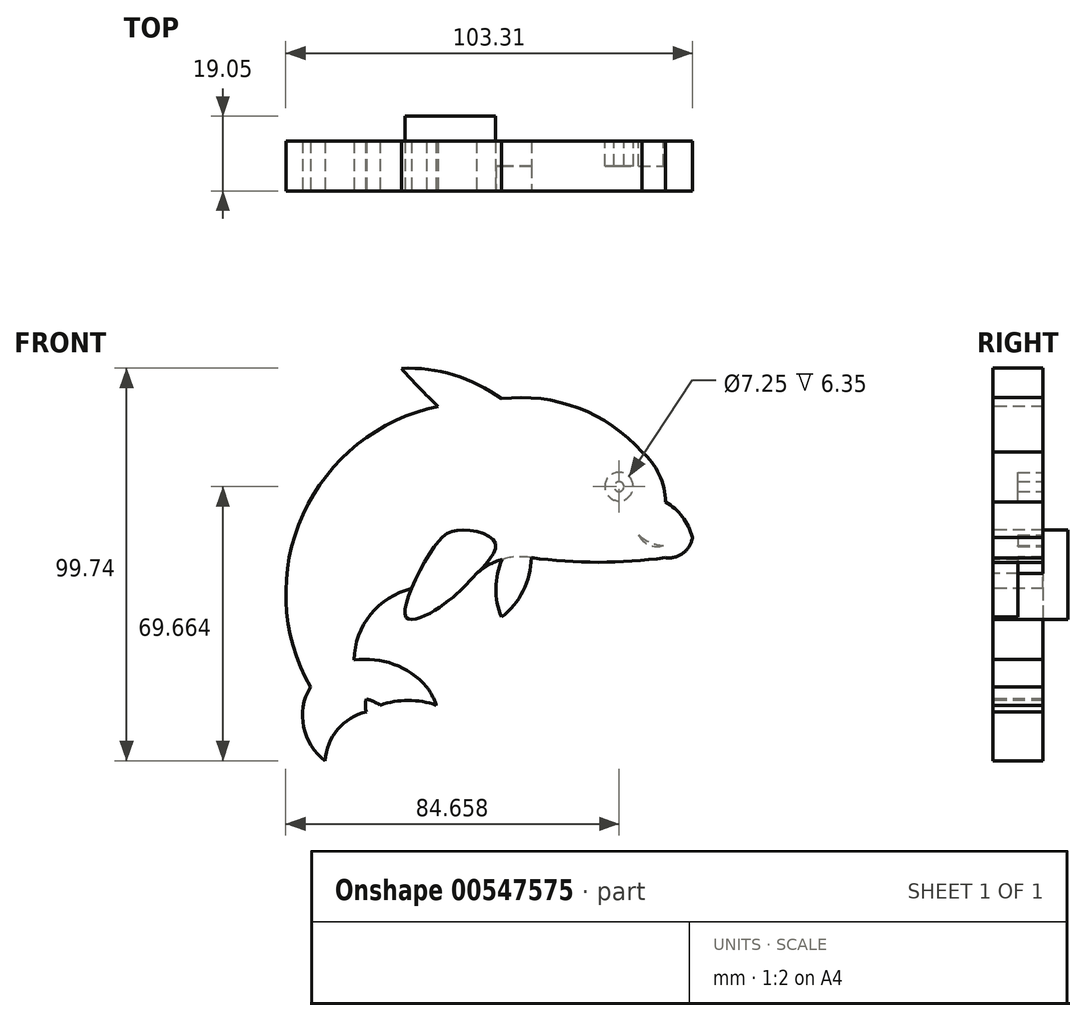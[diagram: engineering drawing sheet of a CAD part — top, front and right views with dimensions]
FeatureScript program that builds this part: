
annotation { "Feature Type Name" : "Feature", "Feature Type Description" : "" }
export const myFeature = defineFeature(function(context is Context, id is Id, definition is map)
    precondition{}
    {
        {
            var Q0;
            Q0=qCreatedBy(makeId("Front.planeOp"),FACE);
            var sketch = newSketch(context, id + "F0", { "sketchPlane" : qUnion([Q0])});
            skArc(sketch, "E0", {"start": v(-21.74, 57.63) * mm, "mid": v(-17.2, 52.68) * mm, "end": v(-12.41, 47.99) * mm});
            skArc(sketch, "E1", {"start": v(3.68, 49.92) * mm, "mid": v(-8.37, 55.95) * mm, "end": v(-21.74, 57.63) * mm});
            skArc(sketch, "E2", {"start": v(39.42, 36.38) * mm, "mid": v(23.22, 47.55) * mm, "end": v(3.68, 49.92) * mm});
            skArc(sketch, "E3", {"start": v(45.32, 23.7) * mm, "mid": v(43.74, 30.68) * mm, "end": v(39.42, 36.38) * mm});
            skArc(sketch, "E4", {"start": v(52.19, 14.71) * mm, "mid": v(49.66, 19.9) * mm, "end": v(45.32, 23.7) * mm});
            skArc(sketch, "E5", {"start": v(45.32, 9.53) * mm, "mid": v(49.83, 10.7) * mm, "end": v(52.19, 14.71) * mm});
            skArc(sketch, "E6", {"start": v(11.27, 9.53) * mm, "mid": v(28.3, 8.38) * mm, "end": v(45.32, 9.53) * mm});
            skArc(sketch, "E7", {"start": v(3.68, -5.58) * mm, "mid": v(9.2, 1.11) * mm, "end": v(11.27, 9.53) * mm});
            skArc(sketch, "E8", {"start": v(3.85, 9.11) * mm, "mid": v(2.26, 1.78) * mm, "end": v(3.68, -5.58) * mm});
            skArc(sketch, "E9", {"start": v(11.27, 9.53) * mm, "mid": v(3.85, 9.11) * mm, "end": v(-2.62, 5.46) * mm});
            skFitSpline(sketch, "E10", {"points": [v(-2.62, 5.46) * mm, v(-8.07, 0) * mm, v(-16.67, -5.6) * mm, v(-20.7, -5.31) * mm, v(-13.95, 11.58) * mm, v(-6.56, 16.6) * mm, v(2.08, 13.23) * mm, v(-2.62, 5.46) * mm]});
            skArc(sketch, "E11", {"start": v(-19.2, 1.68) * mm, "mid": v(-29.6, -4.9) * mm, "end": v(-33.76, -16.47) * mm});
            skArc(sketch, "E12", {"start": v(-15.33, -23.25) * mm, "mid": v(-23.7, -17.54) * mm, "end": v(-33.76, -16.47) * mm});
            skArc(sketch, "E13", {"start": v(-12.9, -27.95) * mm, "mid": v(-13.93, -25.5) * mm, "end": v(-15.33, -23.25) * mm});
            skArc(sketch, "E14", {"start": v(-12.9, -27.95) * mm, "mid": v(-20.03, -26.73) * mm, "end": v(-27.16, -27.95) * mm});
            skArc(sketch, "E15", {"start": v(-27.16, -27.95) * mm, "mid": v(-28.82, -27) * mm, "end": v(-30.64, -26.38) * mm});
            skArc(sketch, "E16", {"start": v(-30.64, -26.38) * mm, "mid": v(-30.9, -28) * mm, "end": v(-30.64, -29.62) * mm});
            skArc(sketch, "E17", {"start": v(-30.64, -29.62) * mm, "mid": v(-37.96, -34.09) * mm, "end": v(-41.1, -42.07) * mm});
            skArc(sketch, "E18", {"start": v(-44.9, -23.37) * mm, "mid": v(-46.6, -33.45) * mm, "end": v(-41.1, -42.07) * mm});
            skArc(sketch, "E19", {"start": v(-12.41, 47.99) * mm, "mid": v(-46.75, 20.55) * mm, "end": v(-44.9, -23.37) * mm});
            skSolve(sketch);
        }
        {
            var Q0;
            Q0=makeQuery(id+"F0.imprint","IMPRINT",FACE,{"disambiguationData":[TD([[makeQuery(id+"F0.imprint","IMPRINT",EDGE,{"derivedFrom":sQuery(id+"F0.wireOp",EDGE,"E0")}),1.0]])]});
            extrude(context, id + "F1", {"entities" : qUnion([Q0]), "oppositeDirection" : true, "depth" : 12.7 * mm, "offsetDistance" : 25.4 * mm});
        }
        {
            var Q0;
            {var subQ0=sQuery(id+"F0.wireOp",EDGE,"E10");var subQ1=makeQuery(id+"F0.imprint","INTERSECT",VERTEX,{"derivedFrom":[sQuery(id+"F0.wireOp",EDGE,"E9"),subQ0]});Q0=makeQuery(id+"F0.imprint","IMPRINT",FACE,{"disambiguationData":[TD([[makeQuery(id+"F0.imprint","IMPRINT",EDGE,{"disambiguationData":[TD([[subQ1,-1.0]])],"derivedFrom":subQ0}),-1.0]])]});}
            extrude(context, id + "F2", {"entities" : qUnion([Q0]), "oppositeDirection" : true, "depth" : 19.05 * mm, "offsetDistance" : 25.4 * mm});
        }
        {
            var Q0;
            {var subQ0=sQuery(id+"F0.wireOp",EDGE,"E7");Q0=makeQuery(id+"F0.imprint","IMPRINT",FACE,{"disambiguationData":[TD([[makeQuery(id+"F0.imprint","IMPRINT",EDGE,{"derivedFrom":subQ0}),1.0]])]});}
            extrude(context, id + "F3", {"entities" : qUnion([Q0]), "operationType" : NewBodyOperationType.ADD, "oppositeDirection" : true, "depth" : 6.35 * mm, "offsetDistance" : 25.4 * mm});
        }
        {
            var Q0;
            Q0=qCreatedBy(makeId("Front.planeOp"),FACE);
            cPlane(context, id + "F4", {"entities" : qUnion([Q0]), "cplaneType" : CPlaneType.OFFSET, "offset" : 12.7 * mm, "oppositeDirection" : true, "width" : 152.4 * mm, "height" : 152.4 * mm});
        }
        {
            var Q0;
            Q0=qCreatedBy(id+"F4.planeOp",FACE);
            var sketch = newSketch(context, id + "F5", { "sketchPlane" : qUnion([Q0])});
            skCircle(sketch, "E20", {"center": v(33.54, 27.6) * mm, "radius": 3.62 * mm});
            skArc(sketch, "E21", {"start": v(38.5, 15.33) * mm, "mid": v(41.15, 12.76) * mm, "end": v(44.84, 12.63) * mm});
            skArc(sketch, "E22", {"start": v(38.5, 15.33) * mm, "mid": v(41.44, 13.43) * mm, "end": v(44.84, 12.63) * mm});
            skCircle(sketch, "E23", {"center": v(33.54, 27.6) * mm, "radius": 1.25 * mm});
            skSolve(sketch);
        }
        {
            var Q0;
            Q0=makeQuery(id+"F5.imprint","IMPRINT",FACE,{"disambiguationData":[TD([[makeQuery(id+"F5.imprint","IMPRINT",EDGE,{"derivedFrom":sQuery(id+"F5.wireOp",EDGE,"E21")}),1.0]])]});
            var Q1;
            Q1=makeQuery(id+"F5.imprint","IMPRINT",FACE,{"disambiguationData":[TD([[makeQuery(id+"F5.imprint","IMPRINT",EDGE,{"derivedFrom":sQuery(id+"F5.wireOp",EDGE,"E20")}),1.0]])]});
            extrude(context, id + "F6", {"entities" : qUnion([Q0, Q1]), "operationType" : NewBodyOperationType.REMOVE, "depth" : 6.35 * mm, "offsetDistance" : 25.4 * mm});
        }
    });
